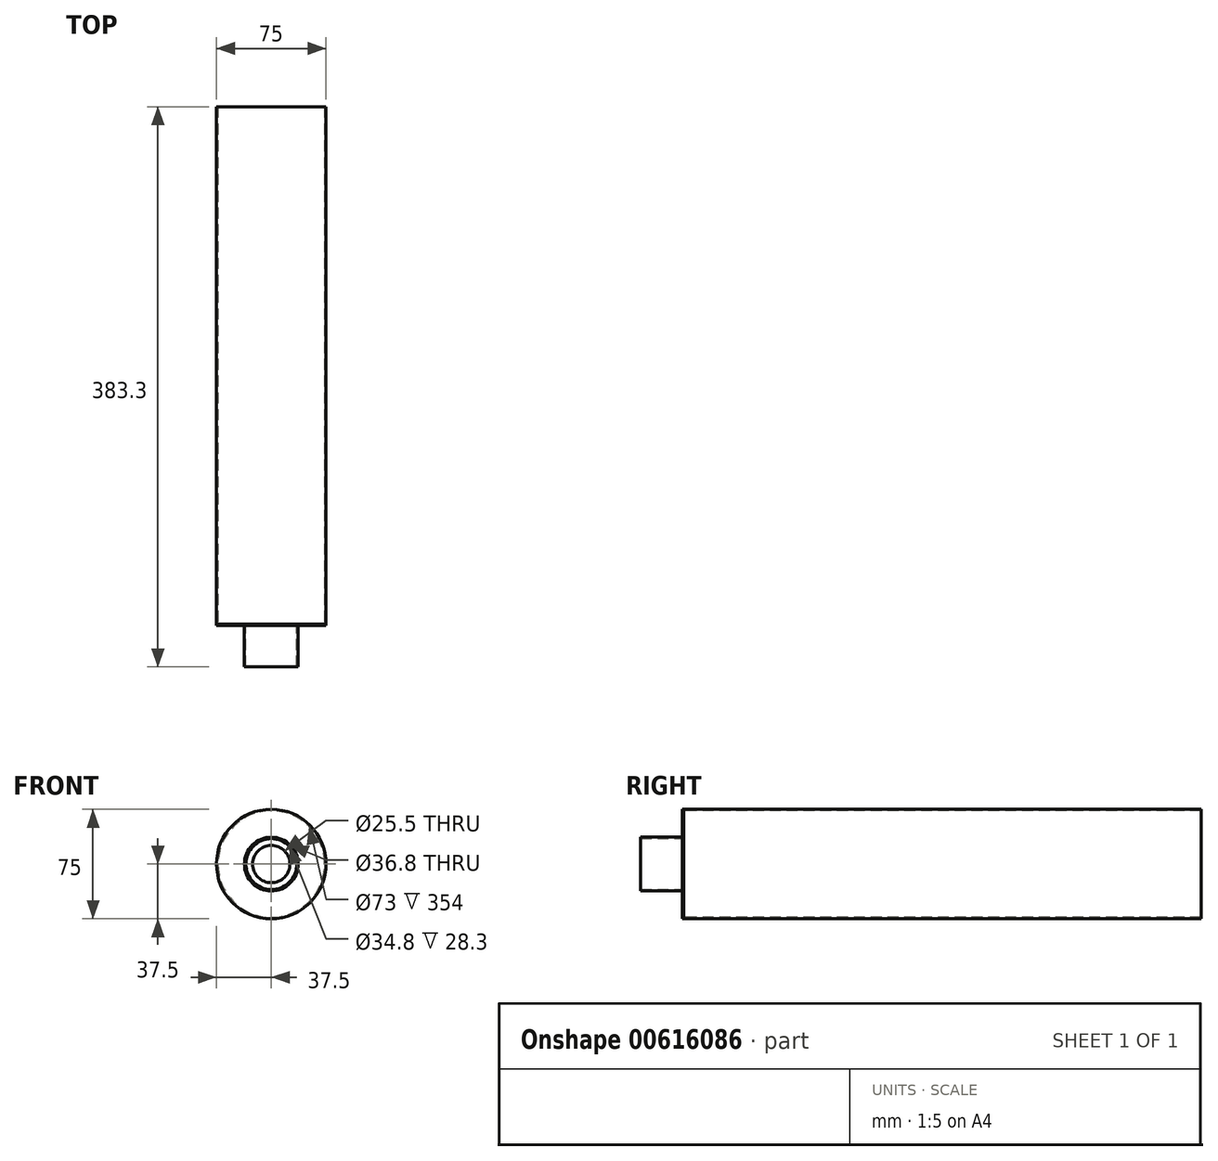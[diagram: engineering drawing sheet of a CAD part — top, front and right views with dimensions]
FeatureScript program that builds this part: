
annotation { "Feature Type Name" : "Feature", "Feature Type Description" : "" }
export const myFeature = defineFeature(function(context is Context, id is Id, definition is map)
    precondition{}
    {
        {
            var Q0;
            Q0=qCreatedBy(makeId("Front.planeOp"),FACE);
            var sketch = newSketch(context, id + "F0", { "sketchPlane" : qUnion([Q0])});
            skCircle(sketch, "E0", {"center": v(0, 0) * mm, "radius": 18.4 * mm});
            skCircle(sketch, "E1", {"center": v(0, 0) * mm, "radius": 17.4 * mm});
            skSolve(sketch);
        }
        {
            var Q0;
            Q0 = qSketchRegion(id + "F0", true);
            extrude(context, id + "F1", {"entities" : qUnion([Q0]), "depth" : 28.3 * mm, "offsetDistance" : 25 * mm});
        }
        {
            var Q0;
            Q0=qCreatedBy(makeId("Front.planeOp"),FACE);
            var sketch = newSketch(context, id + "F2", { "sketchPlane" : qUnion([Q0])});
            skCircle(sketch, "E2", {"center": v(0, 0) * mm, "radius": 18.4 * mm});
            skCircle(sketch, "E3", {"center": v(0, 0) * mm, "radius": 37.5 * mm});
            skSolve(sketch);
        }
        {
            var Q0;
            Q0 = qSketchRegion(id + "F2", true);
            extrude(context, id + "F3", {"entities" : qUnion([Q0]), "depth" : -1 * mm, "offsetDistance" : 25 * mm});
        }
        {
            var Q0;
            Q0=qCreatedBy(makeId("Front.planeOp"),FACE);
            var sketch = newSketch(context, id + "F4", { "sketchPlane" : qUnion([Q0])});
            skCircle(sketch, "E4", {"center": v(0, 0) * mm, "radius": 37.5 * mm});
            skCircle(sketch, "E5", {"center": v(0, 0) * mm, "radius": 36.5 * mm});
            skSolve(sketch);
        }
        {
            var Q0;
            Q0 = qSketchRegion(id + "F4", true);
            extrude(context, id + "F5", {"entities" : qUnion([Q0]), "operationType" : NewBodyOperationType.ADD, "depth" : -355 * mm, "offsetDistance" : 25 * mm});
        }
        {
            var Q0;
            Q0=qCreatedBy(makeId("Front.planeOp"),FACE);
            var sketch = newSketch(context, id + "F6", { "sketchPlane" : qUnion([Q0])});
            skCircle(sketch, "E6.0.0", {"center": v(0, 0) * mm, "radius": 37.5 * mm});
            skCircle(sketch, "E7", {"center": v(0, 0) * mm, "radius": 12.75 * mm});
            skSolve(sketch);
        }
        {
            var Q0;
            Q0=makeQuery(id+"F6.imprint","IMPRINT",FACE,{"disambiguationData":[TD([[makeQuery(id+"F6.imprint","IMPRINT",EDGE,{"derivedFrom":sQuery(id+"F6.wireOp",EDGE,"E6.0.0")}),1.0]])]});
            extrude(context, id + "F7", {"entities" : qUnion([Q0]), "oppositeDirection" : true, "depth" : 1 * mm, "offsetDistance" : 25 * mm});
        }
    });
